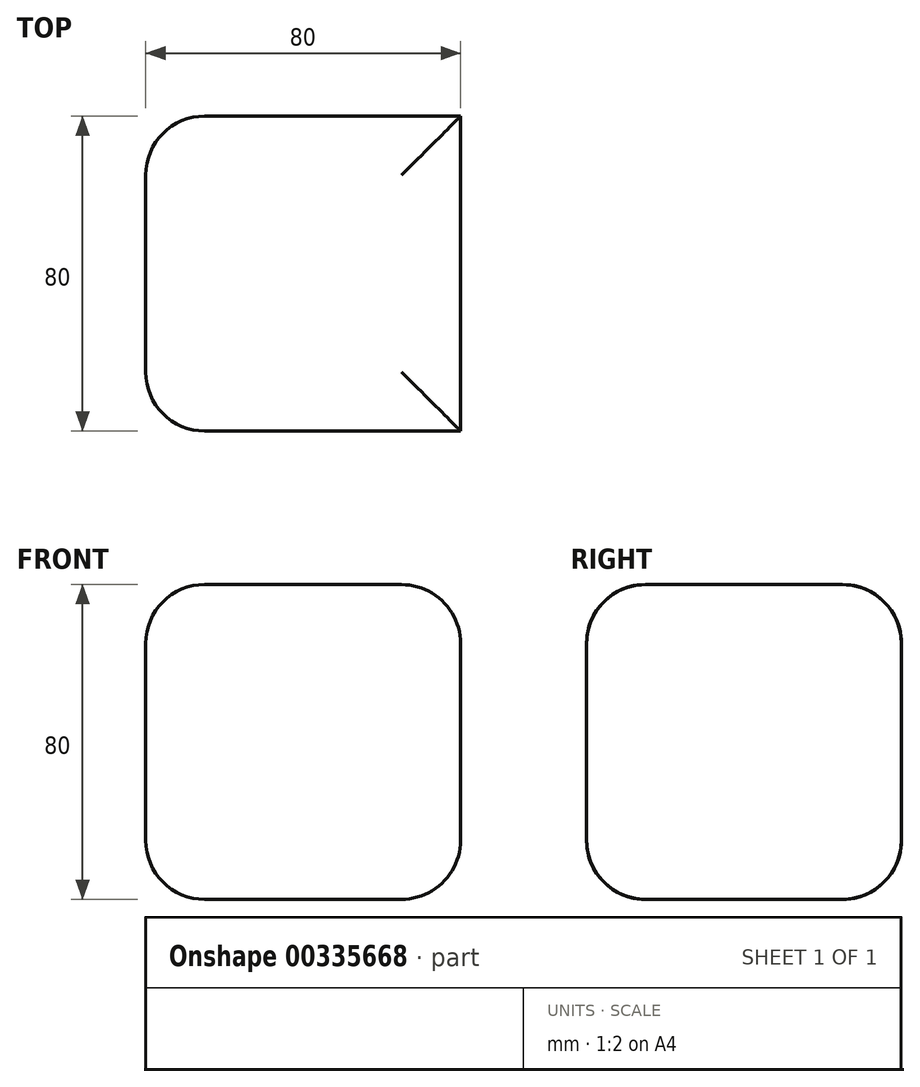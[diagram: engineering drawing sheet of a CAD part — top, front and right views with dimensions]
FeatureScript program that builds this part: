
annotation { "Feature Type Name" : "Feature", "Feature Type Description" : "" }
export const myFeature = defineFeature(function(context is Context, id is Id, definition is map)
    precondition{}
    {
        {
            var Q0;
            Q0=qCreatedBy(makeId("Top.planeOp"),FACE);
            var sketch = newSketch(context, id + "F0", { "sketchPlane" : qUnion([Q0])});
            skLineSegment(sketch, "E0.bottom", {"start": v(40, -40) * mm, "end": v(-40, -40) * mm});
            skLineSegment(sketch, "E0.top", {"start": v(40, 40) * mm, "end": v(-40, 40) * mm});
            skLineSegment(sketch, "E0.left", {"start": v(40, -40) * mm, "end": v(40, 40) * mm});
            skLineSegment(sketch, "E0.right", {"start": v(-40, -40) * mm, "end": v(-40, 40) * mm});
            skPoint(sketch, "E0.middle", {"position": v(0, 0) * mm});
            skSolve(sketch);
        }
        {
            var Q0;
            Q0 = qSketchRegion(id + "F0", true);
            extrude(context, id + "F1", {"entities" : qUnion([Q0]), "endBound" : BoundingType.SYMMETRIC, "depth" : 80 * mm});
        }
        {
            var Q0;
            Q0=makeQuery(id+"F1.opExtrude","CAP_EDGE",EDGE,{"disambiguationData":[OSD([sQuery(id+"F0.wireOp",EDGE,"E0.right")])],"isStart":false});
            var Q1;
            Q1=makeQuery(id+"F1.opExtrude","CAP_EDGE",EDGE,{"disambiguationData":[OSD([sQuery(id+"F0.wireOp",EDGE,"E0.left")])],"isStart":false});
            var Q2;
            Q2=makeQuery(id+"F1.opExtrude","CAP_FACE",FACE,{"disambiguationData":[OSD([sQuery(id+"F0.wireOp",EDGE,"E0.bottom"),sQuery(id+"F0.wireOp",EDGE,"E0.top"),sQuery(id+"F0.wireOp",EDGE,"E0.left"),sQuery(id+"F0.wireOp",EDGE,"E0.right")])],"isStart":false});
            var Q3;
            Q3=makeQuery(id+"F1.opExtrude","SWEPT_FACE",FACE,{"disambiguationData":[OSD([sQuery(id+"F0.wireOp",EDGE,"E0.right")])]});
            var Q4;
            Q4=makeQuery(id+"F1.opExtrude","CAP_EDGE",EDGE,{"disambiguationData":[OSD([sQuery(id+"F0.wireOp",EDGE,"E0.right")])],"isStart":true});
            var Q5;
            Q5=makeQuery(id+"F1.opExtrude","SWEPT_EDGE",EDGE,{"disambiguationData":[OSD([sQuery(id+"F0.wireOp",EDGE,"E0.top"),sQuery(id+"F0.wireOp",EDGE,"E0.right")])]});
            var Q6;
            Q6=makeQuery(id+"F1.opExtrude","SWEPT_EDGE",EDGE,{"disambiguationData":[OSD([sQuery(id+"F0.wireOp",EDGE,"E0.bottom"),sQuery(id+"F0.wireOp",EDGE,"E0.right")])]});
            var Q7;
            Q7=makeQuery(id+"F1.opExtrude","CAP_EDGE",EDGE,{"disambiguationData":[OSD([sQuery(id+"F0.wireOp",EDGE,"E0.top")])],"isStart":true});
            var Q8;
            Q8=makeQuery(id+"F1.opExtrude","CAP_EDGE",EDGE,{"disambiguationData":[OSD([sQuery(id+"F0.wireOp",EDGE,"E0.left")])],"isStart":true});
            var Q9;
            Q9=makeQuery(id+"F1.opExtrude","CAP_EDGE",EDGE,{"disambiguationData":[OSD([sQuery(id+"F0.wireOp",EDGE,"E0.bottom")])],"isStart":true});
            fillet(context, id + "F2", {"entities" : qUnion([Q0, Q1, Q2, Q3, Q4, Q5, Q6, Q7, Q8, Q9]), "radius" : 15 * mm, "tangentPropagation" : true, "allowEdgeOverflow" : false});
        }
    });
